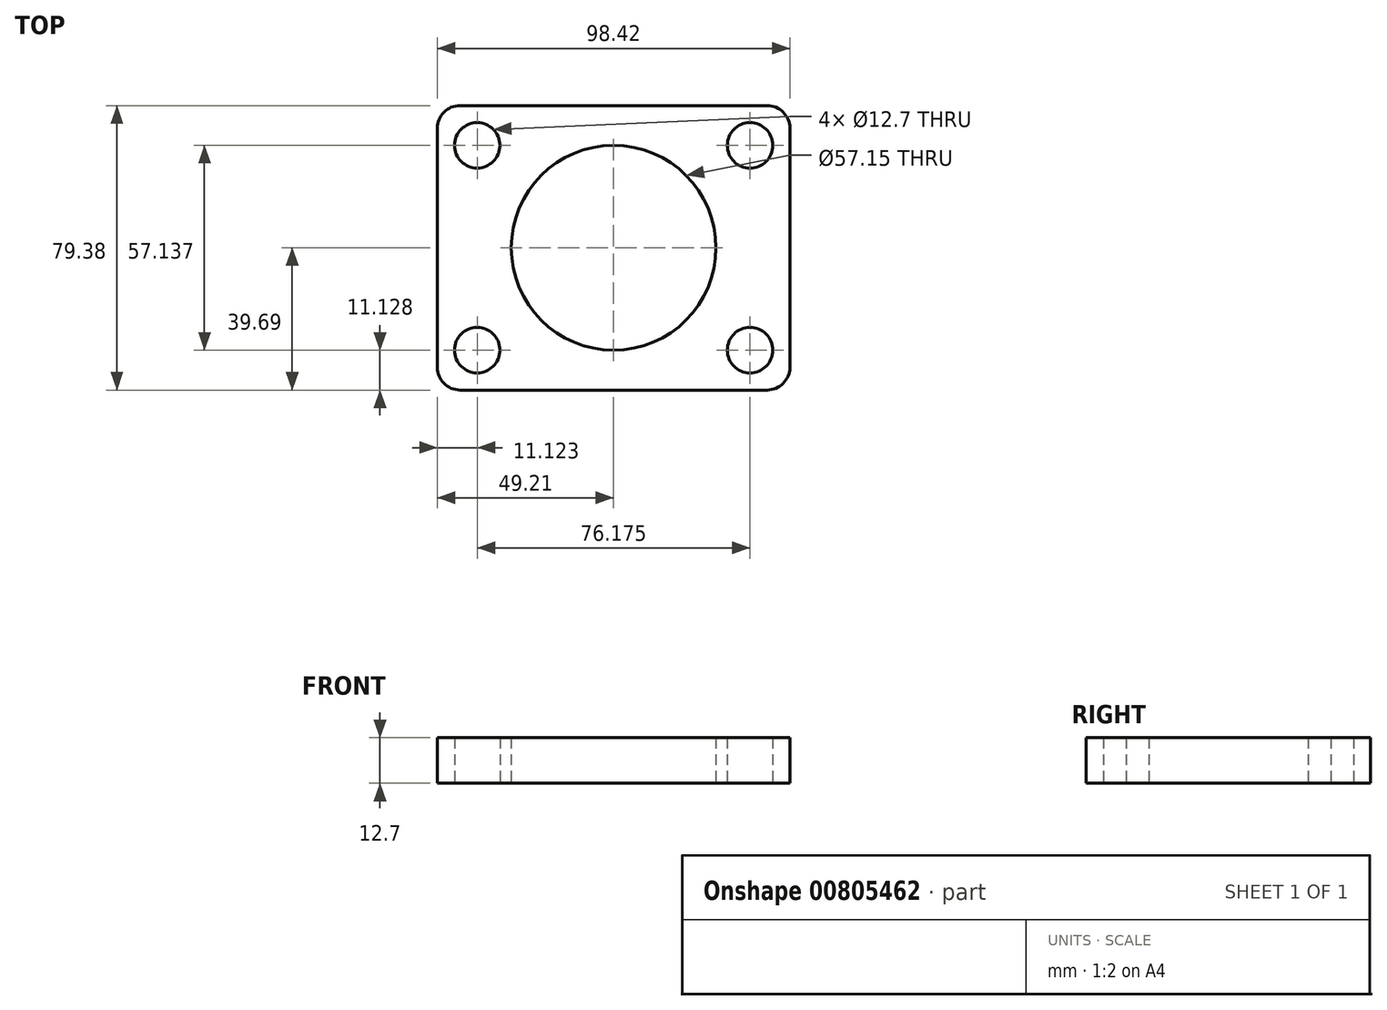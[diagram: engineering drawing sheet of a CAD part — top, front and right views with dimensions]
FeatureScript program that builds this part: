
annotation { "Feature Type Name" : "Feature", "Feature Type Description" : "" }
export const myFeature = defineFeature(function(context is Context, id is Id, definition is map)
    precondition{}
    {
        {
            var Q0;
            Q0=qCreatedBy(makeId("Top.planeOp"),FACE);
            var sketch = newSketch(context, id + "F0", { "sketchPlane" : qUnion([Q0])});
            skCircle(sketch, "E0", {"center": v(0, 0) * mm, "radius": 28.58 * mm});
            skLineSegment(sketch, "E1.bottom", {"start": v(42.86, 39.69) * mm, "end": v(-42.86, 39.69) * mm});
            skLineSegment(sketch, "E1.top", {"start": v(42.86, -39.69) * mm, "end": v(-42.86, -39.69) * mm});
            skLineSegment(sketch, "E1.left", {"start": v(49.21, 33.34) * mm, "end": v(49.21, -33.34) * mm});
            skLineSegment(sketch, "E1.right", {"start": v(-49.21, 33.34) * mm, "end": v(-49.21, -33.34) * mm});
            skCircle(sketch, "E2", {"center": v(-38.09, 28.57) * mm, "radius": 6.35 * mm});
            skCircle(sketch, "E3", {"center": v(38.09, 28.56) * mm, "radius": 6.35 * mm});
            skCircle(sketch, "E4", {"center": v(38.09, -28.56) * mm, "radius": 6.35 * mm});
            skCircle(sketch, "E5", {"center": v(-38.09, -28.56) * mm, "radius": 6.35 * mm});
            skPoint(sketch, "E6.visualSharp", {"position": v(-49.21, 39.69) * mm});
            skArc(sketch, "E6.filletArc", {"start": v(-42.86, 39.69) * mm, "mid": v(-47.35, 37.83) * mm, "end": v(-49.21, 33.34) * mm});
            skPoint(sketch, "E7.visualSharp", {"position": v(49.21, 39.69) * mm});
            skArc(sketch, "E7.filletArc", {"start": v(49.21, 33.34) * mm, "mid": v(47.35, 37.83) * mm, "end": v(42.86, 39.69) * mm});
            skPoint(sketch, "E8.visualSharp", {"position": v(49.21, -39.69) * mm});
            skArc(sketch, "E8.filletArc", {"start": v(42.86, -39.69) * mm, "mid": v(47.35, -37.83) * mm, "end": v(49.21, -33.34) * mm});
            skPoint(sketch, "E9.visualSharp", {"position": v(-49.21, -39.69) * mm});
            skArc(sketch, "E9.filletArc", {"start": v(-49.21, -33.34) * mm, "mid": v(-47.35, -37.83) * mm, "end": v(-42.86, -39.69) * mm});
            skSolve(sketch);
        }
        {
            var Q0;
            Q0 = qSketchRegion(id + "F0", true);
            var Q1;
            Q1=makeQuery(id+"F0.imprint","IMPRINT",FACE,{"disambiguationData":[TD([[makeQuery(id+"F0.imprint","IMPRINT",EDGE,{"derivedFrom":sQuery(id+"F0.wireOp",EDGE,"E0")}),-1.0]])]});
            extrude(context, id + "F1", {"entities" : qUnion([Q0, Q1]), "depth" : 12.7 * mm, "offsetDistance" : 25.4 * mm});
        }
    });
